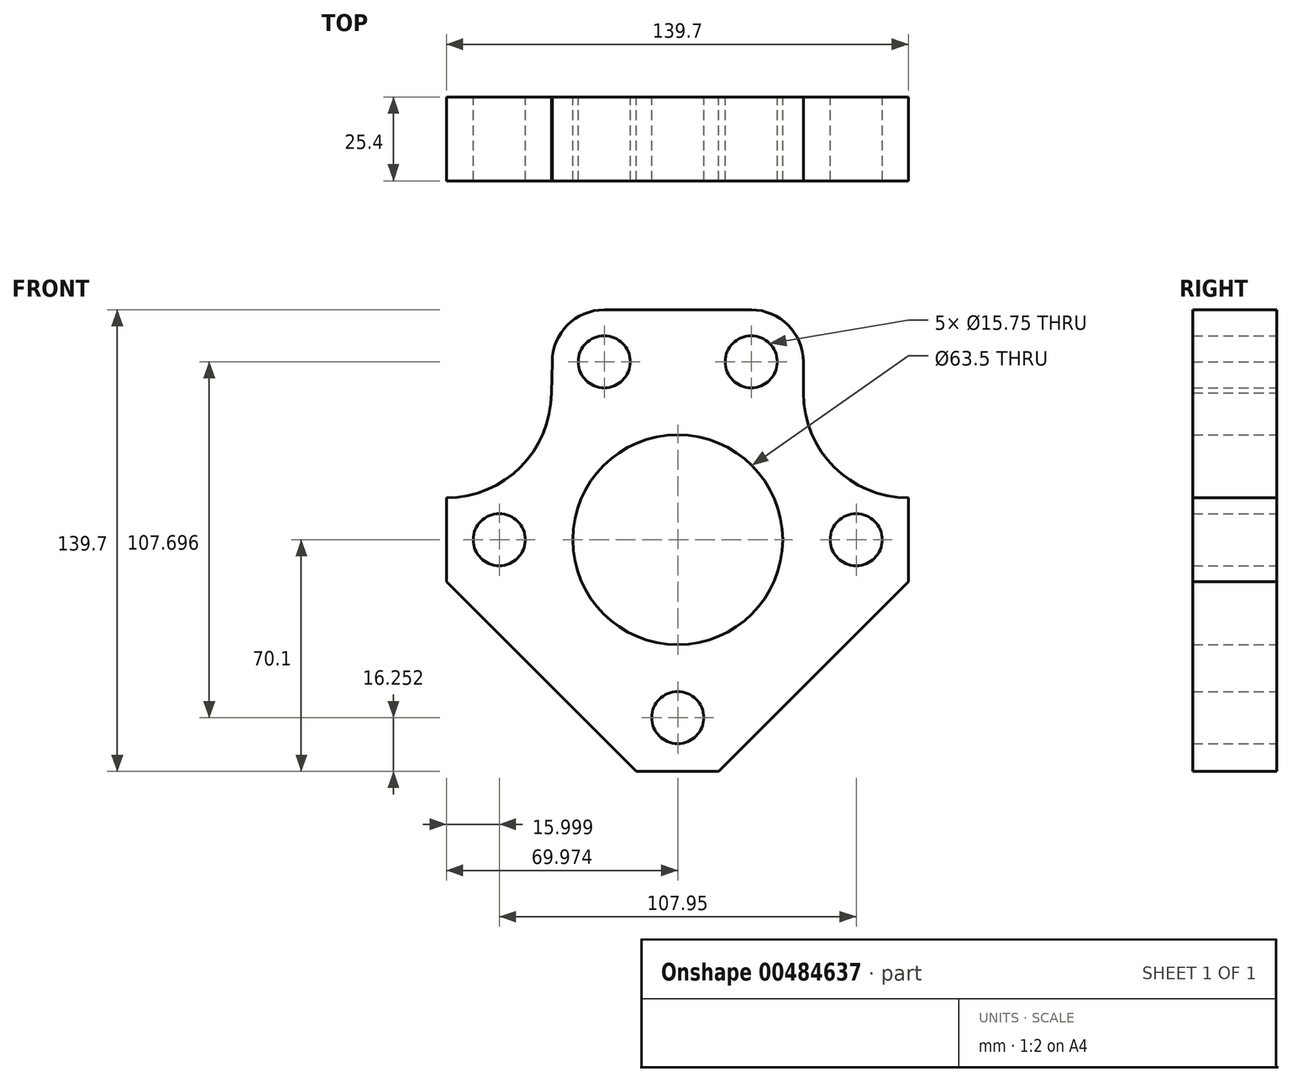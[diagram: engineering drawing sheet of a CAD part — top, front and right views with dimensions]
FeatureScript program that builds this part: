
annotation { "Feature Type Name" : "Feature", "Feature Type Description" : "" }
export const myFeature = defineFeature(function(context is Context, id is Id, definition is map)
    precondition{}
    {
        {
            var Q0;
            Q0=qCreatedBy(makeId("Front.planeOp"),FACE);
            var sketch = newSketch(context, id + "F0", { "sketchPlane" : qUnion([Q0])});
            skLineSegment(sketch, "E0", {"start": v(-15.49, -114.55) * mm, "end": v(9.4, -114.55) * mm});
            skLineSegment(sketch, "E1", {"start": v(9.4, -114.55) * mm, "end": v(66.8, -57.15) * mm});
            skLineSegment(sketch, "E2", {"start": v(66.8, -57.15) * mm, "end": v(66.8, -31.75) * mm});
            skLineSegment(sketch, "E3", {"start": v(-72.9, -31.75) * mm, "end": v(-72.9, -57.15) * mm});
            skLineSegment(sketch, "E4", {"start": v(-72.9, -57.15) * mm, "end": v(-15.49, -114.55) * mm});
            skArc(sketch, "E5.filletArc", {"start": v(-72.9, -31.75) * mm, "mid": v(-50.44, -22.45) * mm, "end": v(-41.14, 0) * mm});
            skArc(sketch, "E6", {"start": v(35.06, 0) * mm, "mid": v(44.36, -22.45) * mm, "end": v(66.8, -31.75) * mm});
            skLineSegment(sketch, "E7", {"start": v(-25.14, 25.15) * mm, "end": v(19.3, 25.15) * mm});
            skArc(sketch, "E8.filletArc", {"start": v(-25.14, 25.15) * mm, "mid": v(-36.28, 20.53) * mm, "end": v(-40.89, 9.4) * mm});
            skArc(sketch, "E9.filletArc", {"start": v(35.06, 9.4) * mm, "mid": v(30.44, 20.53) * mm, "end": v(19.3, 25.15) * mm});
            skCircle(sketch, "E10", {"center": v(-2.92, -44.45) * mm, "radius": 31.75 * mm});
            skCircle(sketch, "E11", {"center": v(51.06, -44.45) * mm, "radius": 7.87 * mm});
            skCircle(sketch, "E12", {"center": v(-56.9, -44.45) * mm, "radius": 7.87 * mm});
            skCircle(sketch, "E13", {"center": v(-25.14, 9.4) * mm, "radius": 7.87 * mm});
            skCircle(sketch, "E14", {"center": v(19.3, 9.4) * mm, "radius": 7.87 * mm});
            skCircle(sketch, "E15", {"center": v(-2.92, -98.3) * mm, "radius": 7.87 * mm});
            skPoint(sketch, "E16", {"position": v(-2.92, 25.15) * mm});
            skPoint(sketch, "E17", {"position": v(66.8, -44.45) * mm});
            skPoint(sketch, "E18", {"position": v(-72.9, -44.45) * mm});
            skPoint(sketch, "E19", {"position": v(-3.04, -114.55) * mm});
            skLineSegment(sketch, "E20", {"start": v(-40.89, 9.4) * mm, "end": v(-41.14, 0) * mm});
            skLineSegment(sketch, "E21", {"start": v(35.06, 9.4) * mm, "end": v(35.06, 0) * mm});
            skSolve(sketch);
        }
        {
            var Q0;
            Q0 = qSketchRegion(id + "F0", true);
            extrude(context, id + "F1", {"entities" : qUnion([Q0]), "depth" : 25.4 * mm});
        }
    });
